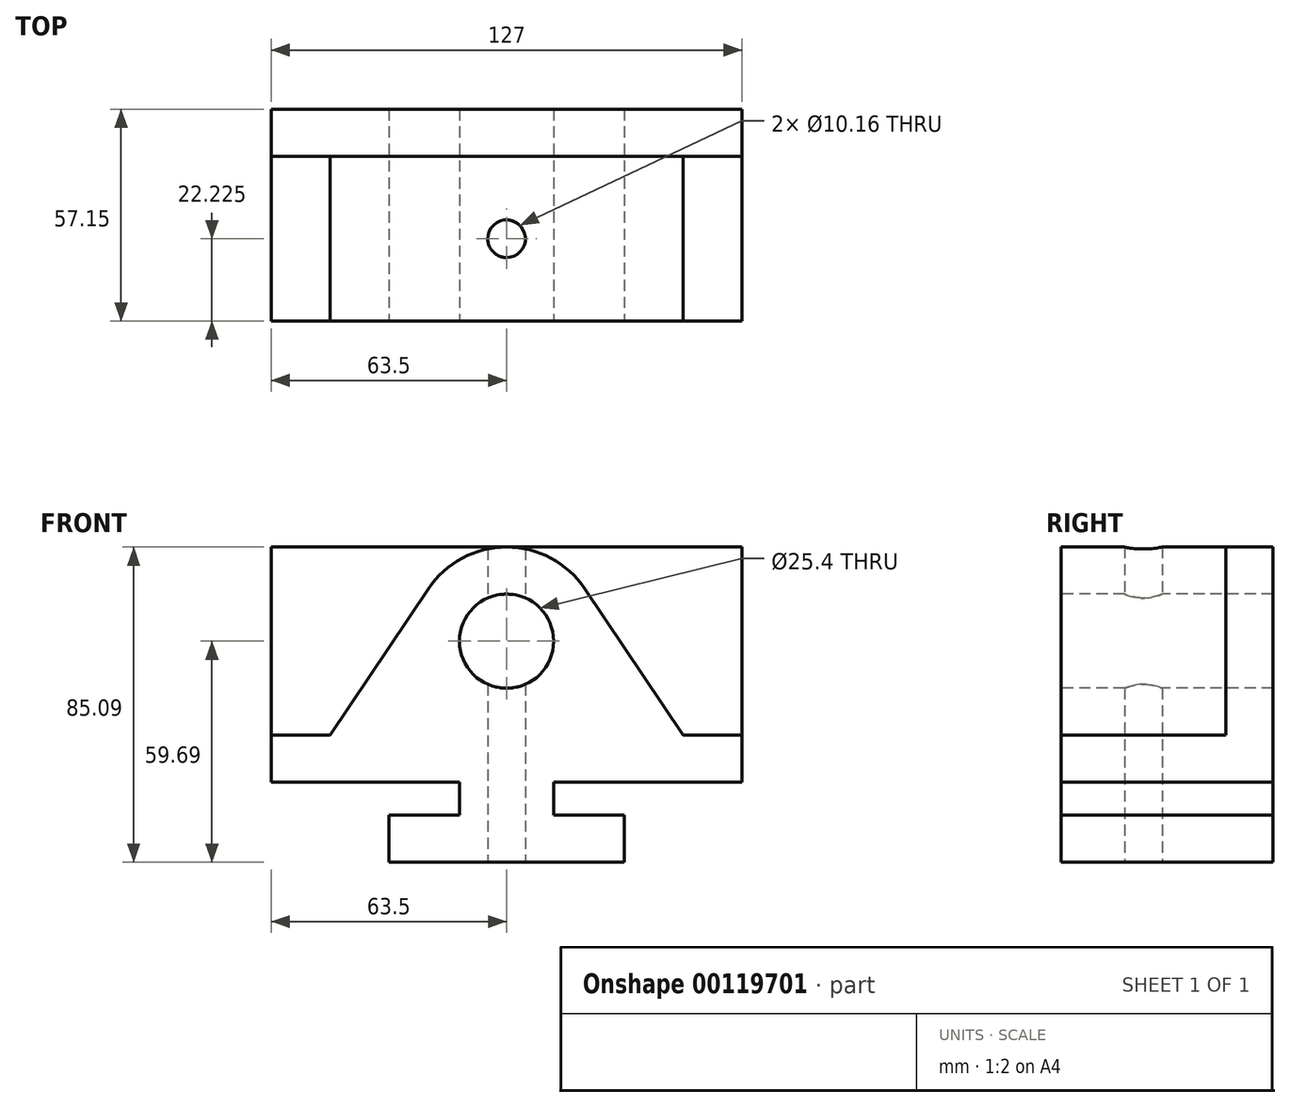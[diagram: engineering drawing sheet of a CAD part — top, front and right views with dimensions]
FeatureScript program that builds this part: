
annotation { "Feature Type Name" : "Feature", "Feature Type Description" : "" }
export const myFeature = defineFeature(function(context is Context, id is Id, definition is map)
    precondition{}
    {
        {
            var Q0;
            Q0=qCreatedBy(makeId("Top.planeOp"),FACE);
            var sketch = newSketch(context, id + "F0", { "sketchPlane" : qUnion([Q0])});
            skLineSegment(sketch, "E0.bottom", {"start": v(0, 0) * mm, "end": v(127, 0) * mm});
            skLineSegment(sketch, "E0.top", {"start": v(0, 57.15) * mm, "end": v(127, 57.15) * mm});
            skLineSegment(sketch, "E0.left", {"start": v(0, 0) * mm, "end": v(0, 57.15) * mm});
            skLineSegment(sketch, "E0.right", {"start": v(127, 0) * mm, "end": v(127, 57.15) * mm});
            skLineSegment(sketch, "E1", {"start": v(31.75, 57.15) * mm, "end": v(31.75, 0) * mm, "construction": true});
            skLineSegment(sketch, "E2", {"start": v(50.8, 57.15) * mm, "end": v(50.8, 0) * mm, "construction": true});
            skLineSegment(sketch, "E3", {"start": v(76.2, 57.15) * mm, "end": v(76.2, 0) * mm, "construction": true});
            skLineSegment(sketch, "E4", {"start": v(95.25, 57.15) * mm, "end": v(95.25, 0) * mm, "construction": true});
            skLineSegment(sketch, "E5", {"start": v(15.87, 57.15) * mm, "end": v(15.87, 0) * mm, "construction": true});
            skLineSegment(sketch, "E6", {"start": v(111.12, 57.15) * mm, "end": v(111.12, 0) * mm, "construction": true});
            skLineSegment(sketch, "E7", {"start": v(63.5, -14.04) * mm, "end": v(63.5, 58.5) * mm, "construction": true});
            skPoint(sketch, "E7.startSnap0", {"position": v(63.5, 0) * mm});
            skCircle(sketch, "E8", {"center": v(63.5, 22.23) * mm, "radius": 5.08 * mm});
            skLineSegment(sketch, "E9", {"start": v(0, 44.45) * mm, "end": v(127, 44.45) * mm, "construction": true});
            skSolve(sketch);
        }
        {
            var Q0;
            Q0 = qSketchRegion(id + "F0", true);
            extrude(context, id + "F1", {"entities" : qUnion([Q0]), "depth" : 85.1 * mm});
        }
        {
            var Q0;
            Q0=makeQuery(id+"F1.opExtrude","SWEPT_FACE",FACE,{"disambiguationData":[OSD([sQuery(id+"F0.wireOp",EDGE,"E0.bottom")])]});
            var sketch = newSketch(context, id + "F2", { "sketchPlane" : qUnion([Q0])});
            skLineSegment(sketch, "E10", {"start": v(0, 34.3) * mm, "end": v(15.87, 34.3) * mm});
            skLineSegment(sketch, "E11", {"start": v(15.87, 34.3) * mm, "end": v(42.4, 73.84) * mm});
            skLineSegment(sketch, "E12", {"start": v(127, 34.3) * mm, "end": v(111.13, 34.3) * mm});
            skLineSegment(sketch, "E13", {"start": v(111.13, 34.3) * mm, "end": v(84.6, 73.84) * mm});
            skArc(sketch, "E14", {"start": v(84.6, 73.84) * mm, "mid": v(63.5, 85.1) * mm, "end": v(42.4, 73.84) * mm});
            skLineSegment(sketch, "E15", {"start": v(63.5, -7.62) * mm, "end": v(63.5, 89.12) * mm, "construction": true});
            skPoint(sketch, "E15.startSnap0", {"position": v(63.5, 0) * mm});
            skPoint(sketch, "E15.endSnap0", {"position": v(63.5, 85.1) * mm});
            skLineSegment(sketch, "E16", {"start": v(0, 34.3) * mm, "end": v(0, 85.1) * mm});
            skLineSegment(sketch, "E17", {"start": v(0, 85.1) * mm, "end": v(127, 85.1) * mm});
            skLineSegment(sketch, "E18", {"start": v(127, 85.1) * mm, "end": v(127, 34.3) * mm});
            skSolve(sketch);
        }
        {
            var Q0;
            Q0 = qSketchRegion(id + "F2", true);
            extrude(context, id + "F3", {"entities" : qUnion([Q0]), "operationType" : NewBodyOperationType.REMOVE, "oppositeDirection" : true, "depth" : 44.45 * mm});
        }
        {
            var Q0;
            Q0=makeQuery(id+"F1.opExtrude","SWEPT_FACE",FACE,{"disambiguationData":[OSD([sQuery(id+"F0.wireOp",EDGE,"E0.bottom")])]});
            var sketch = newSketch(context, id + "F4", { "sketchPlane" : qUnion([Q0])});
            skPoint(sketch, "E19.startSnap0", {"position": v(29.14, 54.07) * mm});
            skLineSegment(sketch, "E20", {"start": v(31.75, 12.7) * mm, "end": v(50.8, 12.7) * mm});
            skLineSegment(sketch, "E21", {"start": v(50.8, 12.7) * mm, "end": v(50.8, 21.6) * mm});
            skLineSegment(sketch, "E22", {"start": v(50.8, 21.6) * mm, "end": v(0, 21.59) * mm});
            skLineSegment(sketch, "E23", {"start": v(95.25, 0) * mm, "end": v(95.25, 12.7) * mm});
            skLineSegment(sketch, "E24", {"start": v(95.25, 12.7) * mm, "end": v(76.2, 12.7) * mm});
            skLineSegment(sketch, "E25", {"start": v(76.2, 12.7) * mm, "end": v(76.2, 21.59) * mm});
            skLineSegment(sketch, "E26", {"start": v(76.2, 21.59) * mm, "end": v(127, 21.59) * mm});
            skLineSegment(sketch, "E27", {"start": v(63.5, -3.63) * mm, "end": v(63.5, 88.52) * mm, "construction": true});
            skPoint(sketch, "E27.startSnap0", {"position": v(63.5, 0) * mm});
            skPoint(sketch, "E27.endSnap0", {"position": v(63.5, 85.1) * mm});
            skLineSegment(sketch, "E28", {"start": v(127, 0) * mm, "end": v(127, 21.59) * mm});
            skLineSegment(sketch, "E29", {"start": v(0, 21.59) * mm, "end": v(0, 0) * mm});
            skLineSegment(sketch, "E30", {"start": v(31.75, 12.7) * mm, "end": v(31.75, 0) * mm});
            skLineSegment(sketch, "E31", {"start": v(0, 0) * mm, "end": v(31.75, 0) * mm});
            skLineSegment(sketch, "E32", {"start": v(95.25, 0) * mm, "end": v(127, 0) * mm});
            skCircle(sketch, "E33", {"center": v(63.5, 59.7) * mm, "radius": 12.7 * mm});
            skSolve(sketch);
        }
        {
            var Q0;
            Q0 = qSketchRegion(id + "F4", true);
            extrude(context, id + "F5", {"entities" : qUnion([Q0]), "operationType" : NewBodyOperationType.REMOVE, "endBound" : BoundingType.THROUGH_ALL, "oppositeDirection" : true, "depth" : 25.4 * mm});
        }
    });
